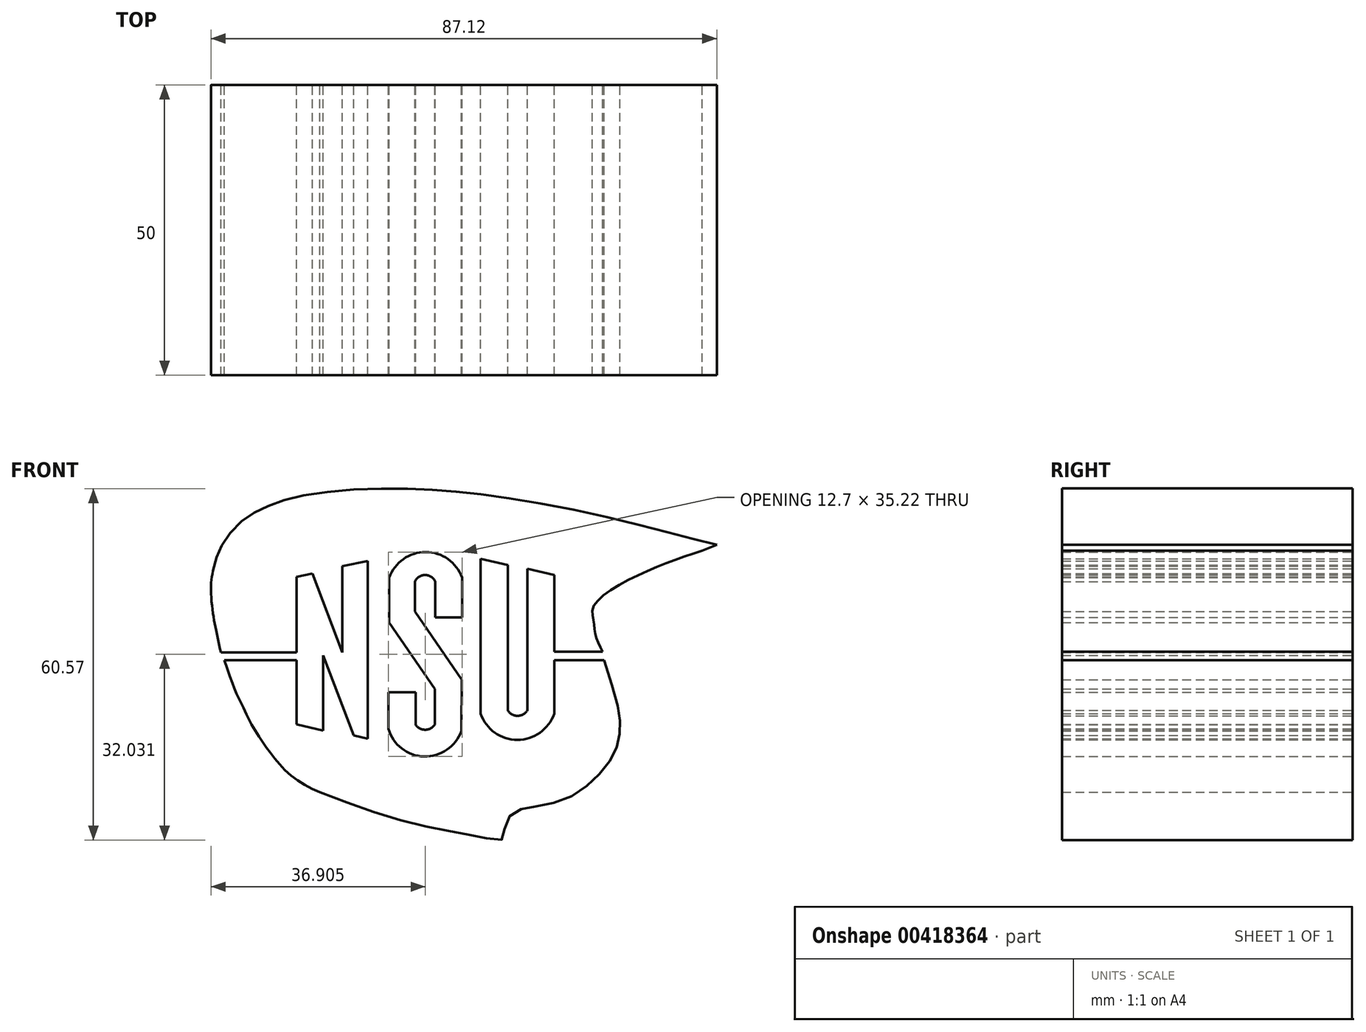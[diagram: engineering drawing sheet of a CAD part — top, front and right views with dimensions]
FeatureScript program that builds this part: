
annotation { "Feature Type Name" : "Feature", "Feature Type Description" : "" }
export const myFeature = defineFeature(function(context is Context, id is Id, definition is map)
    precondition{}
    {
        {
            var Q0;
            Q0=qCreatedBy(makeId("Front.planeOp"),FACE);
            var sketch = newSketch(context, id + "F0", { "sketchPlane" : qUnion([Q0])});
            skLineSegment(sketch, "E0", {"start": v(-37.72, 10.87) * mm, "end": v(-24.7, 10.87) * mm});
            skLineSegment(sketch, "E1", {"start": v(-24.7, 10.87) * mm, "end": v(-24.7, 23.9) * mm});
            skLineSegment(sketch, "E2", {"start": v(-24.7, 23.9) * mm, "end": v(-21.97, 24.44) * mm});
            skLineSegment(sketch, "E3", {"start": v(-21.97, 24.44) * mm, "end": v(-16.82, 10.87) * mm});
            skLineSegment(sketch, "E4", {"start": v(-16.82, 10.87) * mm, "end": v(-16.82, 25.71) * mm});
            skLineSegment(sketch, "E5", {"start": v(-16.82, 25.71) * mm, "end": v(-12.4, 26.58) * mm});
            skLineSegment(sketch, "E6", {"start": v(-12.4, 26.58) * mm, "end": v(-12.4, -3.98) * mm});
            skLineSegment(sketch, "E7", {"start": v(-12.4, -3.98) * mm, "end": v(-14.87, -3.4) * mm});
            skLineSegment(sketch, "E8", {"start": v(-14.87, -3.4) * mm, "end": v(-20.1, 10.36) * mm});
            skLineSegment(sketch, "E9", {"start": v(-20.1, 10.36) * mm, "end": v(-20.1, -2.59) * mm});
            skLineSegment(sketch, "E10", {"start": v(-20.1, -2.59) * mm, "end": v(-24.7, -1.52) * mm});
            skLineSegment(sketch, "E11", {"start": v(-24.7, -1.52) * mm, "end": v(-24.7, 9.54) * mm});
            skLineSegment(sketch, "E12", {"start": v(-24.7, 9.54) * mm, "end": v(-37.13, 9.54) * mm});
            skFitSpline(sketch, "E13", {"points": [v(-37.13, 9.54) * mm, v(-35.8, 5.72) * mm, v(-35.05, 3.85) * mm, v(-33.47, 0.54) * mm, v(-32.56, -1.36) * mm, v(-30.99, -3.88) * mm, v(-29.5, -6) * mm, v(-27.5, -8.54) * mm, v(-24.5, -11.2) * mm, v(-20.7, -13.23) * mm], "startDerivative": vector(11.63, -33.85) * mm, "endDerivative": vector(30.42, -14.2) * mm});
            skFitSpline(sketch, "E14", {"points": [v(-20.7, -13.23) * mm, v(-8.33, -17.56) * mm, v(1.44, -19.87) * mm, v(7.35, -20.99) * mm, v(10.86, -21.24) * mm, v(11.2, -18.76) * mm, v(13.18, -16.45) * mm, v(16, -15.76) * mm, v(21.57, -14.4) * mm, v(25.94, -11.56) * mm, v(29.02, -8.14) * mm, v(30.65, -4.88) * mm, v(31, -1.88) * mm, v(30.74, 1.12) * mm, v(28.25, 9.54) * mm], "startDerivative": vector(108.2, -40.75) * mm, "endDerivative": vector(-32.84, 100.57) * mm});
            skLineSegment(sketch, "E15", {"start": v(28.25, 9.54) * mm, "end": v(19.69, 9.54) * mm});
            skLineSegment(sketch, "E16", {"start": v(19.69, 9.54) * mm, "end": v(19.69, 0.3) * mm});
            skArc(sketch, "E17", {"start": v(7, 0.3) * mm, "mid": v(13.35, -4.19) * mm, "end": v(19.69, 0.3) * mm});
            skLineSegment(sketch, "E18", {"start": v(7, 0.3) * mm, "end": v(7, 1.92) * mm});
            skLineSegment(sketch, "E19", {"start": v(7, 26.96) * mm, "end": v(11.67, 25.9) * mm});
            skLineSegment(sketch, "E20", {"start": v(11.67, 25.9) * mm, "end": v(11.67, 0.88) * mm});
            skLineSegment(sketch, "E21", {"start": v(7, 1.92) * mm, "end": v(7, 26.96) * mm});
            skArc(sketch, "E22", {"start": v(11.67, 0.88) * mm, "mid": v(13.36, -0.04) * mm, "end": v(15.05, 0.88) * mm});
            skLineSegment(sketch, "E23", {"start": v(15.05, 0.88) * mm, "end": v(15.05, 25.27) * mm});
            skLineSegment(sketch, "E24", {"start": v(15.05, 25.27) * mm, "end": v(19.7, 24.2) * mm});
            skLineSegment(sketch, "E25", {"start": v(19.7, 24.2) * mm, "end": v(19.7, 11) * mm});
            skLineSegment(sketch, "E26", {"start": v(19.7, 11) * mm, "end": v(28, 11) * mm});
            skFitSpline(sketch, "E27", {"points": [v(28, 11) * mm, v(26.86, 13.64) * mm, v(26.5, 16.18) * mm, v(26.5, 18.85) * mm, v(34.43, 24.3) * mm, v(45.15, 28.42) * mm], "startDerivative": vector(-8.27, 18.29) * mm, "endDerivative": vector(35.33, 12.01) * mm});
            skFitSpline(sketch, "E28", {"points": [v(45.15, 28.42) * mm, v(47.69, 29.38) * mm], "startDerivative": vector(2.53, 0.96) * mm, "endDerivative": vector(2.53, 0.96) * mm});
            skFitSpline(sketch, "E29", {"points": [v(47.69, 29.38) * mm, v(39.57, 31.47) * mm, v(27.24, 34.53) * mm, v(12.88, 37.28) * mm, v(3.3, 38.5) * mm, v(-4.14, 39.01) * mm, v(-13.33, 39) * mm, v(-22.17, 38.14) * mm, v(-27.44, 36.93) * mm, v(-30.65, 35.6) * mm, v(-33.26, 34.15) * mm, v(-35.74, 31.9) * mm, v(-37.5, 29.38) * mm, v(-38.4, 27.44) * mm, v(-39.1, 24.87) * mm], "startDerivative": vector(-92.78, 23.76) * mm, "endDerivative": vector(-8.75, -48.41) * mm});
            skFitSpline(sketch, "E30", {"points": [v(-37.72, 10.87) * mm, v(-38.56, 14.68) * mm, v(-39.16, 18.13) * mm, v(-39.43, 22.31) * mm, v(-39.1, 24.87) * mm], "startDerivative": vector(-3.39, 14.8) * mm, "endDerivative": vector(2, 11.05) * mm});
            skArc(sketch, "E31", {"start": v(-8.88, -2.29) * mm, "mid": v(-2.74, -7.06) * mm, "end": v(3.67, -2.66) * mm});
            skLineSegment(sketch, "E32", {"start": v(-8.88, -2.29) * mm, "end": v(-8.88, 4) * mm});
            skLineSegment(sketch, "E33", {"start": v(-8.88, 4) * mm, "end": v(-4.18, 4) * mm});
            skLineSegment(sketch, "E34", {"start": v(-4.18, 4) * mm, "end": v(-4.18, -1.58) * mm});
            skArc(sketch, "E35", {"start": v(-4.18, -1.58) * mm, "mid": v(-2.54, -2.45) * mm, "end": v(-0.9, -1.58) * mm});
            skLineSegment(sketch, "E36", {"start": v(-0.9, -1.58) * mm, "end": v(-0.9, -0.8) * mm});
            skLineSegment(sketch, "E37", {"start": v(-0.9, 4.59) * mm, "end": v(-8.74, 16.04) * mm});
            skLineSegment(sketch, "E38", {"start": v(-8.74, 16.04) * mm, "end": v(-8.74, 23.74) * mm});
            skArc(sketch, "E39", {"start": v(3.83, 23.74) * mm, "mid": v(-2.45, 28.16) * mm, "end": v(-8.74, 23.74) * mm});
            skLineSegment(sketch, "E40", {"start": v(3.83, 23.74) * mm, "end": v(3.83, 16.9) * mm});
            skLineSegment(sketch, "E41", {"start": v(3.83, 16.9) * mm, "end": v(-0.8, 16.9) * mm});
            skLineSegment(sketch, "E42", {"start": v(-0.8, 16.9) * mm, "end": v(-0.8, 23.07) * mm});
            skArc(sketch, "E43", {"start": v(-0.8, 23.07) * mm, "mid": v(-2.55, 24.21) * mm, "end": v(-4.3, 23.07) * mm});
            skLineSegment(sketch, "E44", {"start": v(-4.3, 23.07) * mm, "end": v(-4.3, 17.94) * mm});
            skLineSegment(sketch, "E45", {"start": v(-4.3, 17.94) * mm, "end": v(3.74, 6.19) * mm});
            skLineSegment(sketch, "E46", {"start": v(3.74, 6.19) * mm, "end": v(3.67, -2.66) * mm});
            skLineSegment(sketch, "E47", {"start": v(-0.9, -0.8) * mm, "end": v(-0.9, 4.59) * mm});
            skSolve(sketch);
        }
        {
            var Q0;
            Q0=makeQuery(id+"F0.imprint","IMPRINT",FACE,{"disambiguationData":[TD([[makeQuery(id+"F0.imprint","IMPRINT",EDGE,{"derivedFrom":sQuery(id+"F0.wireOp",EDGE,"E0")}),1.0]])]});
            extrude(context, id + "F1", {"entities" : qUnion([Q0]), "depth" : 50 * mm});
        }
    });
